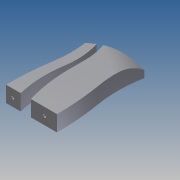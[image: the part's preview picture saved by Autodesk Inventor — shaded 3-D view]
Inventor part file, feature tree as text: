
AUTODESK INVENTOR PART (.ipt)
format: ipt  version: 2014 SP2 (Build 180246200, 246)  size: 168,448 bytes
history: native  units: mm
features: sketch x3, extrude x2, plane x1, sweep x1
ambient origin geometry x8: Origin, YZ Plane, XZ Plane, XY Plane, X Axis, Y Axis, Z Axis, Center Point
bodies: Body1 (feature_tree)
feature tree (7):
  sketch  "Skizze3"  dims[d5=800.0mm d8=450.0mm]
  extrude  "Extrusion2"  Depth=450.0mm
  plane  "Arbeitsebene4"
  sweep  "Sweeping1"
  extrude  "Extrusion3"  Depth=30.0mm
  sketch  "Skizze7"  dims[d9=670.0mm d10=30.0mm]
  sketch  "Skizze8"  dims[d11=40.0mm d12=30.0mm d14=50.0mm d16=130.0mm d18=90.0mm d19=740.0mm d21=90.0mm d22=230.0mm d23=140.0mm d26=100.0mm d28=730.0mm d34=160.0mm d35=30.0mm d36=770.0mm d38=100.0mm d39=140.0mm d40=0.0mm d51=323.428015mm d52=250.0mm d53=2170.0mm d54=450.0mm d55=90.0mm d56=50.0mm d57=50.0mm d58=0.0mm d59=25.0mm d60=70.0mm d61=60.0mm d62=110.0mm d63=100.0mm d64=0.0mm]
